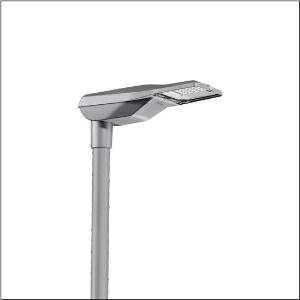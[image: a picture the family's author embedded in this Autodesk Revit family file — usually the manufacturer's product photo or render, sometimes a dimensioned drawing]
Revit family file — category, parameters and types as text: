
# Revit family: streetlight_sl_21_iq_micro___stw1_0a_5xe1e31g08db_041b
name_source: partatom
category: Lighting Fixtures
units: mm (PartAtom-declared; Revit-internal decimal feet)

## family parameters
Cut with Voids When Loaded = No
Host = Face
Light Source = No
Part Type = Normal
Room Calculation Point = No
Round Connector Dimension = Use Diameter
Shared = No

## types (1)
- --- (1 x LED, 4810 lm, 36.4 W, 3000K)
    Apparent Load = 36 VA
    CIE Flux Codes = 38 75 98 100 100
    Color Rendering = 70
    Color Temperature = 3000K
    Default Elevation = 1800 mm
    Description = Streetlight SL 21 iQ micro, mast luminaire, primary light control with lens, of PMMA, primary optical cover: cover, of toughened safety glass, transparent, light distribution: STW1.0a, light emission: direct distribution, primary light characteristic: asymmetric, installation type: post-top, side-entry, LED, High Power LED, rated luminous flux: 4.810lm, luminous efficacy: 132lm/W, light colour: 730, colour temperature: 3000K, control: Street-Remote, Auto-Match, Temp-Guard, Lumen-Switch, Night-Set, Smart-Wire, Light-Fading, Desk-Remote (wireless, voltage-free reading and setting of iQ features in the workshop via application-optimized NFC function/RFID function), optimised constant luminous flux control (CLO 2.0), pre-setting: linear dimming characteristic, mains connection: 220..240V, AC, 50/60Hz, start of lifetime: 36W, end of service life: 38W, reduction: 16W, luminaire housing, of diecast aluminium, powder-coated, Siteco® metallic grey (DB 702S), corrosivity category C5 mid according to DIN EN ISO 12944, please order mast flange separately, inclination adjustable: 0°, 5°, 10°, 15°, sealing non-destructively replaceable, multi-level sealing system, length: 528mm, width: 235mm, height: 110mm, mast flange for spigot size: 42mm (side-entry): 5XC10008XM4, 60/48mm (side-entry/post-top): 5XC10108XM2, 76/60mm (side-entry/post-top): 5XC10108XM1, protection rating (complete): IP66, insulation class (complete): insulation class II (safety insulation), certification: CE, ENEC, ENEC+, VDE, impact resistance: IK09, permissible operating ambient temperature for outdoor applications: -40..+50°C, standard-compliant lighting for roads and squares, packaging unit: 1 piece

Light Distribution: STW1.0a
    Height = 110 mm
    Lamp = 1 x LED
    Lamp Light Flux = 4810 lm
    Lamp Power = 36.4 W
    Lamp count = 1
    Length = 528 mm
    Luminous efficacy = 132 lm/W
    Manufacturer = Siteco
    ModVariant = No
    Model = 5XE1E31G08DB
    Number of Poles = 1
    OnlyDefault = Yes
    Power Factor = 1
    Product Name = Streetlight SL 21 iQ micro | STW1.0a
    Product group = mast luminaire | pylon top
    ProductGroupID = 6100
    Protection Class = Protection class II
    Protection Degree = IP 66
    RLX_Detail_Level = 1
    RLX_Emergency_Light_Flux = 0 lm
    RLX_Emergency_Type = 0
    RLX_Emergency_Type_DB = No
    RlxData = <blob elided: 99093 chars, md5=bdab7574>
    Socket = socket
    Standby Power = 0 W
    System Light Flux = 4810 lm
    System Power = 36 W
    Type Comments = factory setting: luminous flux: 100 % | dim-lin: 254 | 715 mA
    Type Image = l_1006881.jpg
    URL = http://relux.com
    VarID = @adj_125833
    Voltage = 0 V
    Weight = 0.00 kg
    Width = 235 mm

## geometry (parser evidence)
native form markers: Blend x4, Sweep x9
no freeform markers — native parametric forms only
